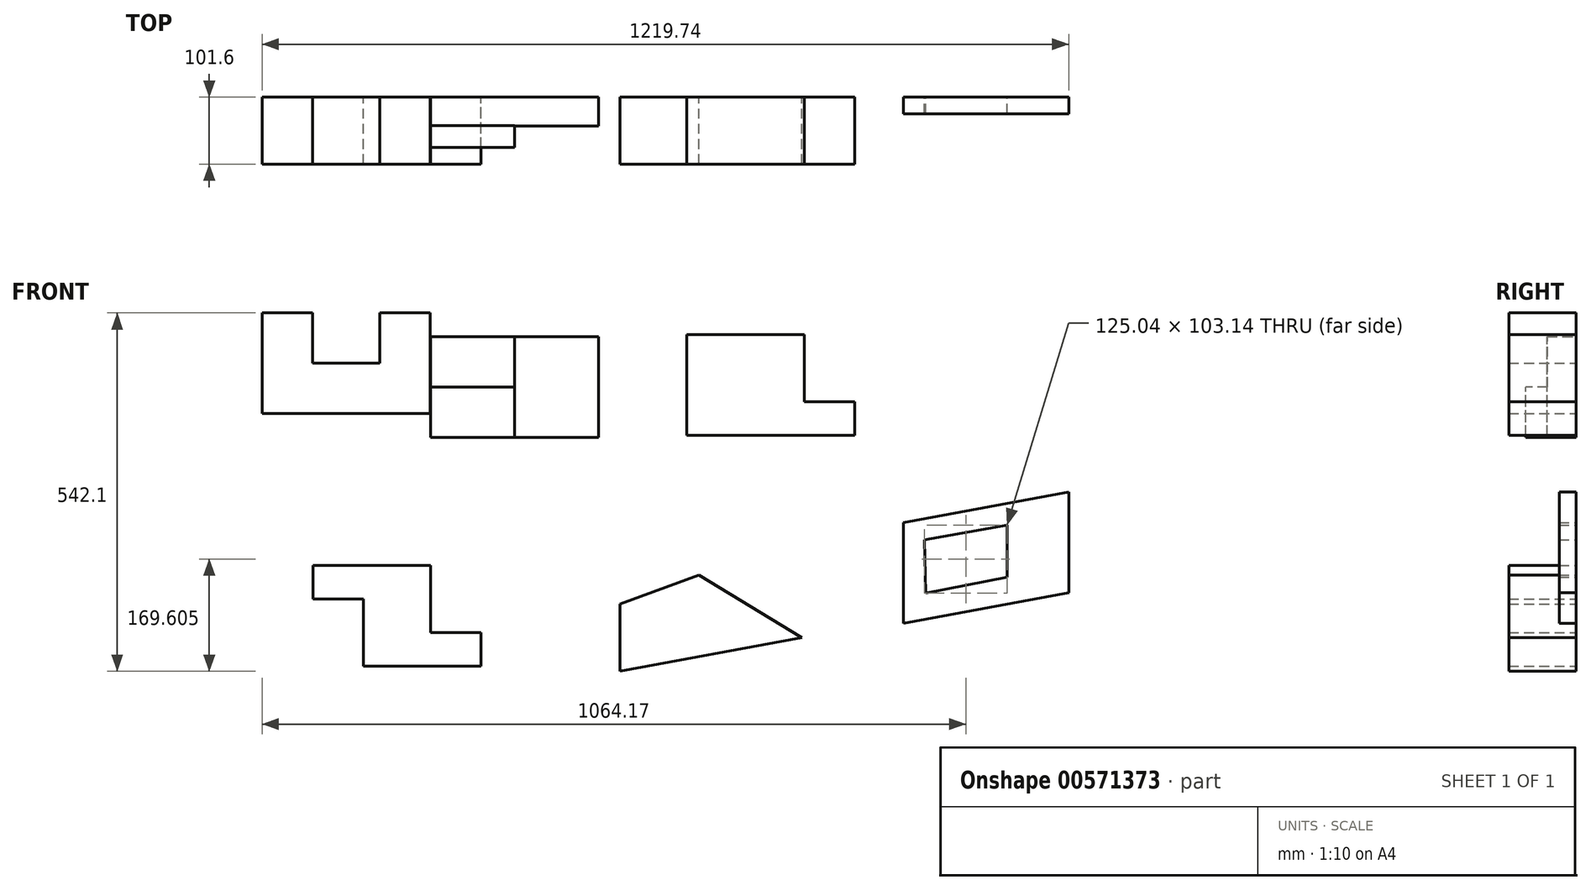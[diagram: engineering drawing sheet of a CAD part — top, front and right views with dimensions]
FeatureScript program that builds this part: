
annotation { "Feature Type Name" : "Feature", "Feature Type Description" : "" }
export const myFeature = defineFeature(function(context is Context, id is Id, definition is map)
    precondition{}
    {
        {
            var Q0;
            Q0=qCreatedBy(makeId("Front.planeOp"),FACE);
            var sketch = newSketch(context, id + "F0", { "sketchPlane" : qUnion([Q0])});
            skLineSegment(sketch, "E0", {"start": v(254, 152.4) * mm, "end": v(254, 0) * mm});
            skLineSegment(sketch, "E1", {"start": v(177.8, 152.4) * mm, "end": v(177.8, 76.2) * mm});
            skLineSegment(sketch, "E2", {"start": v(177.8, 76.2) * mm, "end": v(76.2, 76.2) * mm});
            skLineSegment(sketch, "E3", {"start": v(76.2, 76.2) * mm, "end": v(76.2, 152.4) * mm});
            skLineSegment(sketch, "E4", {"start": v(76.2, 152.4) * mm, "end": v(0, 152.4) * mm});
            skLineSegment(sketch, "E5", {"start": v(0, 152.4) * mm, "end": v(0, 0) * mm});
            skLineSegment(sketch, "E6", {"start": v(0, 0) * mm, "end": v(254, 0) * mm});
            skLineSegment(sketch, "E7", {"start": v(177.8, 152.4) * mm, "end": v(254, 152.4) * mm});
            skSolve(sketch);
        }
        {
            var Q0;
            Q0=makeQuery(id+"F0.imprint","IMPRINT",FACE,{"disambiguationData":[TD([[makeQuery(id+"F0.imprint","IMPRINT",EDGE,{"derivedFrom":sQuery(id+"F0.wireOp",EDGE,"E0")}),-1.0]])]});
            extrude(context, id + "F1", {"entities" : qUnion([Q0]), "depth" : 101.6 * mm, "offsetDistance" : 25.4 * mm});
        }
        {
            var Q0;
            Q0=qCreatedBy(makeId("Front.planeOp"),FACE);
            var sketch = newSketch(context, id + "F2", { "sketchPlane" : qUnion([Q0])});
            skLineSegment(sketch, "E8.bottom", {"start": v(254.8, -35.94) * mm, "end": v(508.8, -35.94) * mm});
            skLineSegment(sketch, "E8.top", {"start": v(254.8, 116.46) * mm, "end": v(508.8, 116.46) * mm});
            skLineSegment(sketch, "E8.left", {"start": v(254.8, -35.94) * mm, "end": v(254.8, 116.46) * mm});
            skLineSegment(sketch, "E8.right", {"start": v(508.8, -35.94) * mm, "end": v(508.8, 116.46) * mm});
            skSolve(sketch);
        }
        {
            var Q0;
            Q0=makeQuery(id+"F2.imprint","IMPRINT",FACE,{"disambiguationData":[TD([[makeQuery(id+"F2.imprint","IMPRINT",EDGE,{"derivedFrom":sQuery(id+"F2.wireOp",EDGE,"E8.bottom")}),1.0]])]});
            extrude(context, id + "F3", {"entities" : qUnion([Q0]), "depth" : 76.2 * mm, "offsetDistance" : 25.4 * mm});
        }
        {
            var Q0;
            Q0=makeQuery(id+"F3.opExtrude","SWEPT_FACE",FACE,{"disambiguationData":[OSD([sQuery(id+"F2.wireOp",EDGE,"E8.top")])]});
            var sketch = newSketch(context, id + "F4", { "sketchPlane" : qUnion([Q0])});
            skLineSegment(sketch, "E9", {"start": v(508.8, -43.62) * mm, "end": v(381.8, -43.62) * mm});
            skLineSegment(sketch, "E10", {"start": v(381.8, -43.62) * mm, "end": v(381.8, -76.2) * mm});
            skSolve(sketch);
        }
        {
            var Q0;
            {var subQ0=sQuery(id+"F4.wireOp",EDGE,"E9");Q0=makeQuery(id+"F4.imprint","IMPRINT",FACE,{"disambiguationData":[TD([[makeQuery(id+"F4.imprint","IMPRINT",EDGE,{"derivedFrom":subQ0}),1.0]])]});}
            extrude(context, id + "F5", {"entities" : qUnion([Q0]), "operationType" : NewBodyOperationType.REMOVE, "oppositeDirection" : true, "depth" : 152.4 * mm, "offsetDistance" : 25.4 * mm});
        }
        {
            var Q0;
            Q0=makeQuery(id+"F3.opExtrude","CAP_FACE",FACE,{"disambiguationData":[OSD([sQuery(id+"F2.wireOp",EDGE,"E8.bottom"),sQuery(id+"F2.wireOp",EDGE,"E8.top"),sQuery(id+"F2.wireOp",EDGE,"E8.left"),sQuery(id+"F2.wireOp",EDGE,"E8.right")])],"isStart":false});
            var sketch = newSketch(context, id + "F6", { "sketchPlane" : qUnion([Q0])});
            skLineSegment(sketch, "E11", {"start": v(254.8, 40.26) * mm, "end": v(381.8, 40.26) * mm});
            skSolve(sketch);
        }
        {
            var Q0;
            {var subQ0=sQuery(id+"F6.wireOp",EDGE,"E11");Q0=makeQuery(id+"F6.imprint","IMPRINT",FACE,{"disambiguationData":[TD([[makeQuery(id+"F6.imprint","IMPRINT",EDGE,{"derivedFrom":subQ0}),1.0]])]});}
            extrude(context, id + "F7", {"entities" : qUnion([Q0]), "operationType" : NewBodyOperationType.REMOVE, "oppositeDirection" : true, "depth" : 33.02 * mm, "offsetDistance" : 25.4 * mm});
        }
        {
            var Q0;
            Q0=qCreatedBy(makeId("Front.planeOp"),FACE);
            var sketch = newSketch(context, id + "F8", { "sketchPlane" : qUnion([Q0])});
            skLineSegment(sketch, "E12", {"start": v(642.26, 119.55) * mm, "end": v(820.06, 119.55) * mm});
            skLineSegment(sketch, "E13", {"start": v(820.06, 119.55) * mm, "end": v(820.06, 17.95) * mm});
            skLineSegment(sketch, "E14", {"start": v(820.06, 17.95) * mm, "end": v(896.26, 17.95) * mm});
            skLineSegment(sketch, "E15", {"start": v(896.26, 17.95) * mm, "end": v(896.26, -32.85) * mm});
            skLineSegment(sketch, "E16", {"start": v(896.26, -32.85) * mm, "end": v(642.26, -32.85) * mm});
            skLineSegment(sketch, "E17", {"start": v(642.26, -32.85) * mm, "end": v(642.26, 119.55) * mm});
            skLineSegment(sketch, "E18", {"start": v(693.06, -32.85) * mm, "end": v(693.06, 119.55) * mm});
            skSolve(sketch);
        }
        {
            var Q0;
            {var subQ1=sQuery(id+"F8.wireOp",EDGE,"E13");Q0=makeQuery(id+"F8.imprint","IMPRINT",FACE,{"disambiguationData":[TD([[makeQuery(id+"F8.imprint","IMPRINT",EDGE,{"derivedFrom":subQ1}),-1.0]])]});}
            var Q1;
            {var subQ0=sQuery(id+"F8.wireOp",EDGE,"E17");Q1=makeQuery(id+"F8.imprint","IMPRINT",FACE,{"disambiguationData":[TD([[makeQuery(id+"F8.imprint","IMPRINT",EDGE,{"derivedFrom":subQ0}),-1.0]])]});}
            extrude(context, id + "F9", {"entities" : qUnion([Q0, Q1]), "depth" : 101.6 * mm, "offsetDistance" : 25.4 * mm});
        }
        {
            var Q0;
            Q0=qCreatedBy(makeId("Front.planeOp"),FACE);
            var sketch = newSketch(context, id + "F10", { "sketchPlane" : qUnion([Q0])});
            skLineSegment(sketch, "E19", {"start": v(76.89, -229.66) * mm, "end": v(254.69, -229.66) * mm});
            skLineSegment(sketch, "E20", {"start": v(254.69, -229.66) * mm, "end": v(254.69, -331.26) * mm});
            skLineSegment(sketch, "E21", {"start": v(254.69, -331.26) * mm, "end": v(330.89, -331.26) * mm});
            skLineSegment(sketch, "E22", {"start": v(330.89, -331.26) * mm, "end": v(330.89, -382.06) * mm});
            skLineSegment(sketch, "E23", {"start": v(330.89, -382.06) * mm, "end": v(153.09, -382.06) * mm});
            skLineSegment(sketch, "E24", {"start": v(153.09, -382.06) * mm, "end": v(153.09, -280.46) * mm});
            skLineSegment(sketch, "E25", {"start": v(153.09, -280.46) * mm, "end": v(76.89, -280.46) * mm});
            skLineSegment(sketch, "E26", {"start": v(76.89, -280.46) * mm, "end": v(76.89, -229.66) * mm});
            skSolve(sketch);
        }
        {
            var Q0;
            Q0=makeQuery(id+"F10.imprint","IMPRINT",FACE,{"disambiguationData":[TD([[makeQuery(id+"F10.imprint","IMPRINT",EDGE,{"derivedFrom":sQuery(id+"F10.wireOp",EDGE,"E19")}),-1.0]])]});
            extrude(context, id + "F11", {"entities" : qUnion([Q0]), "depth" : 101.6 * mm, "offsetDistance" : 25.4 * mm});
        }
        {
            var Q0;
            Q0=qCreatedBy(makeId("Front.planeOp"),FACE);
            var sketch = newSketch(context, id + "F12", { "sketchPlane" : qUnion([Q0])});
            skLineSegment(sketch, "E27", {"start": v(541.22, -288.1) * mm, "end": v(660.47, -244.41) * mm});
            skLineSegment(sketch, "E28", {"start": v(541.22, -288.1) * mm, "end": v(541.22, -389.7) * mm});
            skLineSegment(sketch, "E29", {"start": v(541.22, -389.7) * mm, "end": v(815.96, -338.9) * mm});
            skPoint(sketch, "E29.endSnap0", {"position": v(541.22, -338.9) * mm});
            skLineSegment(sketch, "E30", {"start": v(660.47, -244.41) * mm, "end": v(815.96, -338.9) * mm});
            skSolve(sketch);
        }
        {
            var Q0;
            Q0=makeQuery(id+"F12.imprint","IMPRINT",FACE,{"disambiguationData":[TD([[makeQuery(id+"F12.imprint","IMPRINT",EDGE,{"derivedFrom":sQuery(id+"F12.wireOp",EDGE,"E27")}),-1.0]])]});
            extrude(context, id + "F13", {"entities" : qUnion([Q0]), "depth" : 101.6 * mm, "offsetDistance" : 25.4 * mm});
        }
        {
            var Q0;
            Q0=qCreatedBy(makeId("Front.planeOp"),FACE);
            var sketch = newSketch(context, id + "F14", { "sketchPlane" : qUnion([Q0])});
            skLineSegment(sketch, "E31", {"start": v(1219.74, -118.8) * mm, "end": v(1219.74, -271.2) * mm});
            skLineSegment(sketch, "E32", {"start": v(1219.74, -118.8) * mm, "end": v(970, -165.16) * mm});
            skLineSegment(sketch, "E33", {"start": v(970, -165.16) * mm, "end": v(970, -317.56) * mm});
            skLineSegment(sketch, "E34", {"start": v(970, -317.56) * mm, "end": v(1219.74, -271.2) * mm});
            skLineSegment(sketch, "E35", {"start": v(1001.65, -190.73) * mm, "end": v(1126.7, -168.53) * mm});
            skLineSegment(sketch, "E36", {"start": v(1126.7, -168.53) * mm, "end": v(1126.7, -247.75) * mm});
            skLineSegment(sketch, "E37", {"start": v(1126.7, -247.75) * mm, "end": v(1003.16, -271.66) * mm});
            skLineSegment(sketch, "E38", {"start": v(1003.16, -271.66) * mm, "end": v(1001.65, -190.73) * mm});
            skSolve(sketch);
        }
        {
            var Q0;
            Q0=makeQuery(id+"F14.imprint","IMPRINT",FACE,{"disambiguationData":[TD([[makeQuery(id+"F14.imprint","IMPRINT",EDGE,{"derivedFrom":sQuery(id+"F14.wireOp",EDGE,"E31")}),-1.0]])]});
            extrude(context, id + "F15", {"entities" : qUnion([Q0]), "depth" : 25.4 * mm, "offsetDistance" : 25.4 * mm});
        }
    });
